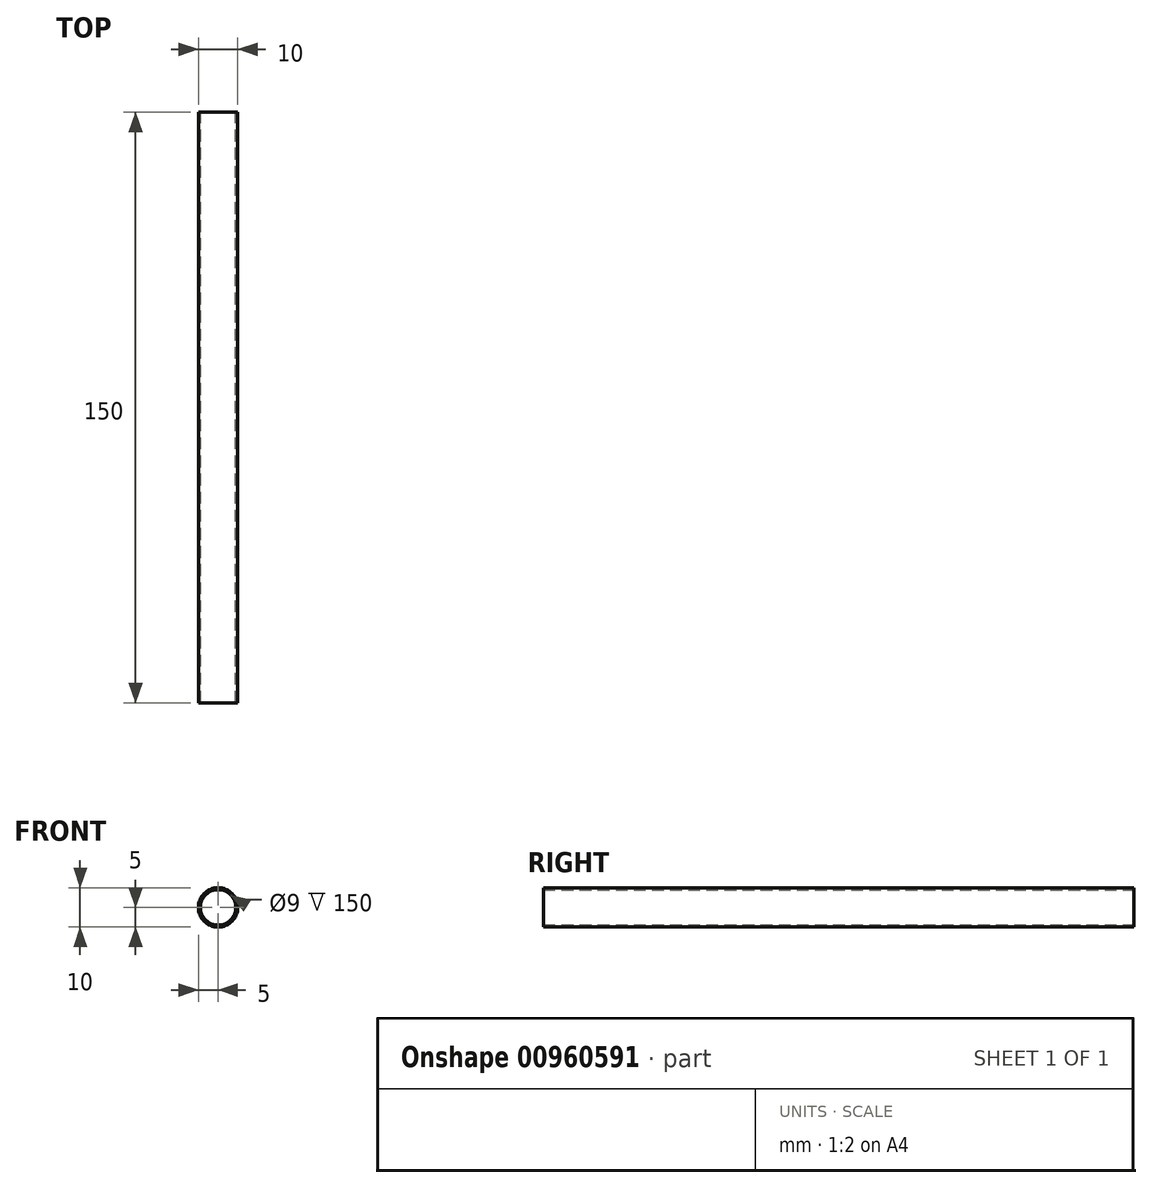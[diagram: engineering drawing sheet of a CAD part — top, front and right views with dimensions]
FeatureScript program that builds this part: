
annotation { "Feature Type Name" : "Feature", "Feature Type Description" : "" }
export const myFeature = defineFeature(function(context is Context, id is Id, definition is map)
    precondition{}
    {
        {
            var Q0;
            Q0=qCreatedBy(makeId("Front.planeOp"),FACE);
            var sketch = newSketch(context, id + "F0", { "sketchPlane" : qUnion([Q0])});
            skCircle(sketch, "E0", {"center": v(0, 0) * mm, "radius": 5 * mm});
            skCircle(sketch, "E1", {"center": v(0, 0) * mm, "radius": 4.5 * mm});
            skSolve(sketch);
        }
        {
            var Q0;
            Q0=makeQuery(id+"F0.imprint","IMPRINT",FACE,{"disambiguationData":[TD([[makeQuery(id+"F0.imprint","IMPRINT",EDGE,{"derivedFrom":sQuery(id+"F0.wireOp",EDGE,"E0")}),1.0]])]});
            extrude(context, id + "F1", {"entities" : qUnion([Q0]), "depth" : 150 * mm, "offsetDistance" : 25 * mm});
        }
    });
